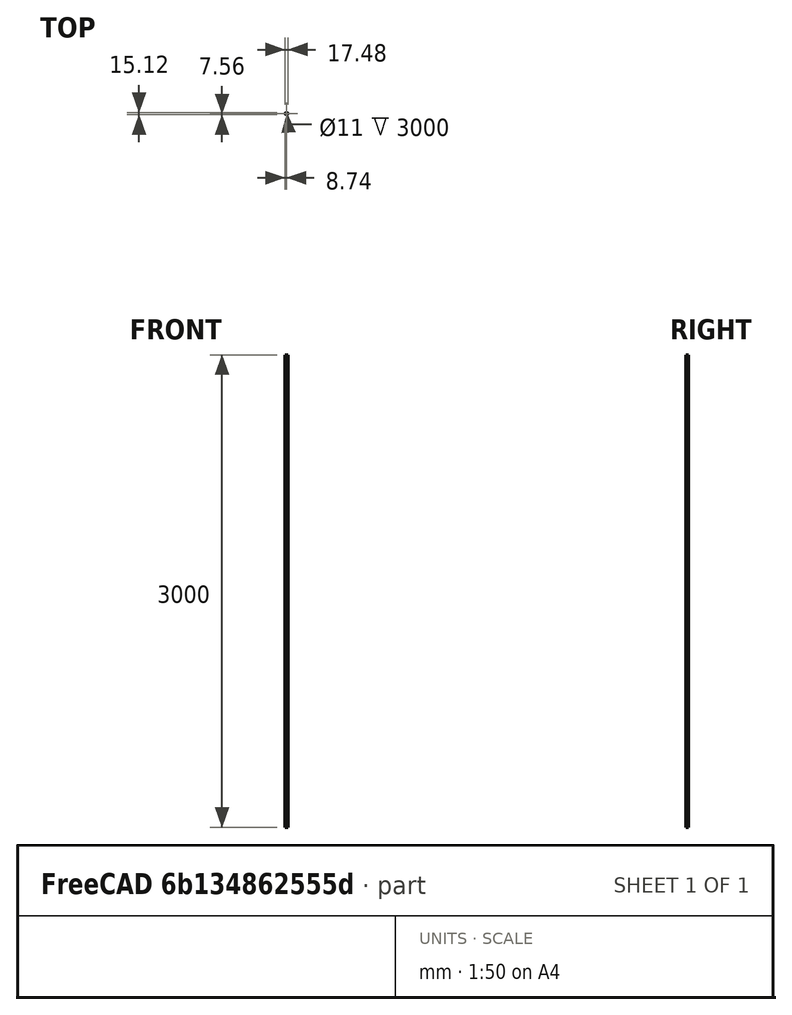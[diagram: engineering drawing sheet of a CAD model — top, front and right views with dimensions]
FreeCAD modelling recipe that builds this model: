
FCSTD DOCUMENT  (FreeCAD 0.21R33771 (Git))
Label: pincellGeometry
License: All rights reserved
LicenseURL: http://en.wikipedia.org/wiki/All_rights_reserved
objects: Part::FeaturePython×7, App::DocumentObjectGroupPython×2, Sketcher::SketchObject×1, PartDesign::Pad×1, PartDesign::Body×1, App::MaterialObjectPython×1, Part::Cylinder×1, Fem::FemMeshObject×1
note: 12 computed .brp shape members not serialized (recipe doc carries the construction recipe); baked Part::Feature solids carry a one-line shape summary decoded from their .brp

FEATURE [Sketcher::SketchObject] Sketch
  FullyConstrained = true
  MapMode = 5
  Support = -> [XY_Plane]
  sketch-geometry (8):
    g0: LineSegment StartX=8.735 StartY=0 StartZ=0 EndX=4.3675 EndY=7.56473 EndZ=0
    g1: LineSegment StartX=4.3675 StartY=7.56473 StartZ=0 EndX=-4.3675 EndY=7.56473 EndZ=0
    g2: LineSegment StartX=-4.3675 StartY=7.56473 StartZ=0 EndX=-8.735 EndY=-9e-16 EndZ=0
    g3: LineSegment StartX=-8.735 StartY=-9e-16 StartZ=0 EndX=-4.3675 EndY=-7.56473 EndZ=0
    g4: LineSegment StartX=-4.3675 StartY=-7.56473 StartZ=0 EndX=4.3675 EndY=-7.56473 EndZ=0
    g5: LineSegment StartX=4.3675 StartY=-7.56473 StartZ=0 EndX=8.735 EndY=0 EndZ=0
    g6: Circle CenterX=0 CenterY=0 CenterZ=0 NormalX=0 NormalY=0 NormalZ=1 AngleXU=0 Radius=8.735
    g7: Circle CenterX=0 CenterY=0 CenterZ=0 NormalX=0 NormalY=0 NormalZ=1 AngleXU=0 Radius=5.5
  constraints (18):
    c: Coincident(g0,g1)
    c: Coincident(g1,g2)
    c: Coincident(g2,g3)
    c: Coincident(g3,g4)
    c: Coincident(g4,g5)
    c: Coincident(g5,g0)
    c: Equal(g0, g1-g5) x5
    c: PointOnObject(g0,g6)
    c: PointOnObject(g1,g6)
    c: PointOnObject(g2,g6)
    c: PointOnObject(g3,g6)
    c: PointOnObject(g4,g6)
    c: PointOnObject(g5,g6)
    c: Coincident(g6,g-1)
    c: PointOnObject(g5,g-1)
    c: Diameter(g6) = 17.47
    c: Coincident(g7,g6)
    c: Diameter(g7) = 11
FEATURE [PartDesign::Pad] Pad
  Direction = (0,0,1)
  Length = 3000
  Length2 = 10
  Profile = -> Sketch
  ReferenceAxis = -> Sketch [N_Axis]
  Type = 0
FEATURE [PartDesign::Body] Body
  Group = -> [Sketch,Pad]
  Origin = -> Origin
  Tip = -> Pad
FEATURE [Part::FeaturePython] PhysicsModel  # WARN: FeaturePython — macro-defined, semantics opaque (R4)
  Flow = 1
  Phase = 0
  SRFModelAxis = (0,0,0)
  SRFModelCoR = (0,0,0)
  SRFModelEnabled = false
  SRFModelRPM = 0
  Time = 0
  Turbulence = 1
  TurbulenceModel = 0
  gx = 0
  gy = 0
  gz = -9800
FEATURE [App::MaterialObjectPython] FluidProperties  label="Water"  # material (typed FeaturePython)
  Category = 1
  Material = CardName=AirCompressible; Cp=1004.703 J/kg/K; Description=Compressible air properties; MolarMass=0.0289643897748887 kg/mol; Name=Air; SutherlandRefTemperature=273.15 K; SutherlandRefViscosity=1.716e-5 kg/m/s; SutherlandTemperature=110.4 K; Type=Compressible
FEATURE [Part::FeaturePython] InitialiseFields  # WARN: FeaturePython — macro-defined, semantics opaque (R4)
  PotentialFlow = true
  PotentialFlowP = false
  Pressure = 100
  ReThetat = 1
  Temperature = 290
  UseInletTemperatureValue = false
  UseInletTurbulenceValues = false
  UseInletUValues = false
  UseOutletPValue = false
  Ux = 0
  Uy = 0
  Uz = 10
  epsilon = 50000000
  gammaInt = 1
  k = 10000
  nuTilda = 55000000
  nut = 50000000
  omega = 1
FEATURE [Part::FeaturePython] CfdSolver  # WARN: FeaturePython — macro-defined, semantics opaque (R4)
  ConvergenceTol = 0.001
  EndTime = 1
  InputCaseName = case
  MaxCFLNumber = 5
  MaxInterfaceCFLNumber = 5
  MaxIterations = 2000
  Parallel = true
  ParallelCores = 4
  PurgeWrite = 0
  StartFrom = 0
  SteadyWriteInterval = 100
  TimeStep = 0.001
  TransientWriteInterval = 0.1
FEATURE [Part::FeaturePython] CfdFluidBoundary  label="constraint"  # WARN: FeaturePython — macro-defined, semantics opaque (R4)
  BoundarySubType = 15
  BoundaryType = 4
  DefaultBoundary = false
  DissipationRate = 50000000
  HeatFlux = 0
  HeatTransferCoeff = 0
  Intermittency = 1
  MassFlowRate = 0
  NuTilda = 55000000
  PeriodicCentreOfRotation = (0,0,0)
  PeriodicCentreOfRotationAxis = (0,0,0)
  PeriodicMaster = true
  PeriodicSeparationVector = (0,0,0)
  PorousBaffleMethod = 0
  Pressure = 100
  PressureDropCoeff = 0
  ReThetat = 1
  RelativeToFrame = false
  ReverseNormal = false
  RotationalPeriodic = false
  RoughnessConstant = 0.5
  RoughnessHeight = 0
  ScreenSpacing = 2
  ScreenWireDiameter = 0.2
  ShapeRefs = -> [Pad]
  SlipRatio = 0
  SpecificDissipationRate = 1
  Temperature = 290
  ThermalBoundaryType = 0
  TurbulenceInletSpecification = 2
  TurbulenceIntensityPercentage = 1
  TurbulenceLengthScale = 100
  TurbulentKineticEnergy = 10000
  TurbulentViscosity = 50000000
  Ux = 0
  Uy = 0
  Uz = 0
  VelocityIsCartesian = true
  VelocityMag = 0
  VolFlowRate = 0
  kEqnTurbulentKineticEnergy = 10000
  kEqnTurbulentViscosity = 50000000
FEATURE [Part::FeaturePython] CfdFluidBoundary002  label="inlet"  # WARN: FeaturePython — macro-defined, semantics opaque (R4)
  BoundarySubType = 5
  BoundaryType = 1
  DefaultBoundary = false
  DissipationRate = 50000000
  HeatFlux = 0
  HeatTransferCoeff = 0
  Intermittency = 1
  MassFlowRate = 0
  NuTilda = 55000000
  PeriodicCentreOfRotation = (0,0,0)
  PeriodicCentreOfRotationAxis = (0,0,0)
  PeriodicMaster = true
  PeriodicSeparationVector = (0,0,0)
  PorousBaffleMethod = 0
  Pressure = 100
  PressureDropCoeff = 0
  ReThetat = 1
  RelativeToFrame = false
  ReverseNormal = false
  RotationalPeriodic = false
  RoughnessConstant = 0.5
  RoughnessHeight = 0
  ScreenSpacing = 2
  ScreenWireDiameter = 0.2
  ShapeRefs = -> [Pad]
  SlipRatio = 0
  SpecificDissipationRate = 1
  Temperature = 800
  ThermalBoundaryType = 0
  TurbulenceInletSpecification = 2
  TurbulenceIntensityPercentage = 1
  TurbulenceLengthScale = 100
  TurbulentKineticEnergy = 10000
  TurbulentViscosity = 50000000
  Ux = 0
  Uy = 0
  Uz = 1000
  VelocityIsCartesian = true
  VelocityMag = 0
  VolFlowRate = 0
  kEqnTurbulentKineticEnergy = 10000
  kEqnTurbulentViscosity = 50000000
FEATURE [Part::FeaturePython] CfdFluidBoundary003  label="outlet"  # WARN: FeaturePython — macro-defined, semantics opaque (R4)
  BoundarySubType = 10
  BoundaryType = 2
  DefaultBoundary = false
  DissipationRate = 50000000
  HeatFlux = 0
  HeatTransferCoeff = 0
  Intermittency = 1
  MassFlowRate = 0
  NuTilda = 55000000
  PeriodicCentreOfRotation = (0,0,0)
  PeriodicCentreOfRotationAxis = (0,0,0)
  PeriodicMaster = true
  PeriodicSeparationVector = (0,0,0)
  PorousBaffleMethod = 0
  Pressure = 0
  PressureDropCoeff = 0
  ReThetat = 1
  RelativeToFrame = false
  ReverseNormal = false
  RotationalPeriodic = false
  RoughnessConstant = 0.5
  RoughnessHeight = 0
  ScreenSpacing = 2
  ScreenWireDiameter = 0.2
  ShapeRefs = -> [Pad]
  SlipRatio = 0
  SpecificDissipationRate = 1
  Temperature = 1200
  ThermalBoundaryType = 0
  TurbulenceInletSpecification = 2
  TurbulenceIntensityPercentage = 1
  TurbulenceLengthScale = 100
  TurbulentKineticEnergy = 10000
  TurbulentViscosity = 50000000
  Ux = 0
  Uy = 0
  Uz = 0
  VelocityIsCartesian = true
  VelocityMag = 0
  VolFlowRate = 0
  kEqnTurbulentKineticEnergy = 10000
  kEqnTurbulentViscosity = 50000000
FEATURE [Part::Cylinder] Cylinder
  Angle = 360
  AttacherType = Attacher::AttachEngine3D
  FirstAngle = 0
  Height = 3000
  Radius = 5.5
  SecondAngle = 0
FEATURE [Part::FeaturePython] CfdFluidBoundary001  label="wall"  # WARN: FeaturePython — macro-defined, semantics opaque (R4)
  BoundarySubType = 0
  BoundaryType = 0
  DefaultBoundary = false
  DissipationRate = 50000000
  HeatFlux = 18000
  HeatTransferCoeff = 0
  Intermittency = 1
  MassFlowRate = 0
  NuTilda = 55000000
  PeriodicCentreOfRotation = (0,0,0)
  PeriodicCentreOfRotationAxis = (0,0,0)
  PeriodicMaster = true
  PeriodicSeparationVector = (0,0,0)
  PorousBaffleMethod = 0
  Pressure = 100
  PressureDropCoeff = 0
  ReThetat = 1
  RelativeToFrame = false
  ReverseNormal = false
  RotationalPeriodic = false
  RoughnessConstant = 0.5
  RoughnessHeight = 0
  ScreenSpacing = 2
  ScreenWireDiameter = 0.2
  ShapeRefs = -> [Cylinder]
  SlipRatio = 0
  SpecificDissipationRate = 1
  Temperature = 290
  ThermalBoundaryType = 2
  TurbulenceInletSpecification = 2
  TurbulenceIntensityPercentage = 1
  TurbulenceLengthScale = 100
  TurbulentKineticEnergy = 10000
  TurbulentViscosity = 50000000
  Ux = 0
  Uy = 0
  Uz = 0
  VelocityIsCartesian = true
  VelocityMag = 0
  VolFlowRate = 0
  kEqnTurbulentKineticEnergy = 10000
  kEqnTurbulentViscosity = 50000000
FEATURE [Fem::FemMeshObject] Pad_MeshSurfaceMesh
FEATURE [App::DocumentObjectGroupPython] Pad_Mesh  # scripted group (container) (typed FeaturePython)
  CaseName = meshCase
  CellsBetweenLevels = 3
  CharacteristicLengthMax = 0.8
  ConvertToDualMesh = false
  EdgeRefinement = 1
  ElementDimension = 1
  Group = -> [Pad_MeshSurfaceMesh]
  ImplicitEdgeDetection = false
  MeshUtility = 0
  NumberOfProcesses = 1
  NumberOfThreads = 0
  Part = -> Pad
  PointInMesh = x=0 m; y=0 m; z=0 m
  STLAngularMeshDensity = 100
  STLRelativeLinearDeflection = 0.001
FEATURE [App::DocumentObjectGroupPython] CfdAnalysis  # scripted group (container) (typed FeaturePython)
  Group = -> [PhysicsModel,FluidProperties,InitialiseFields,CfdSolver,CfdFluidBoundary,CfdFluidBoundary001,CfdFluidBoundary002,CfdFluidBoundary003,Pad_Mesh]
  HostfileName = ../mpi_hostfile
  IsActiveAnalysis = true
  NeedsCaseRewrite = true
  NeedsMeshRerun = false
  NeedsMeshRewrite = true
  UseHostfile = false
